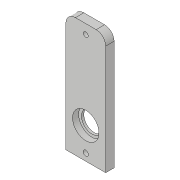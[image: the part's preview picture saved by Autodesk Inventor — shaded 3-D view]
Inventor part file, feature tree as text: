
AUTODESK INVENTOR PART (.ipt)
format: ipt  version: 2018.3 (Build 223284000, 284)  size: 190,976 bytes
history: native  units: in
note: dims shown in document units (in); Inventor stores cm internally (conversion verified against a paired STEP export)
features: extrude x4, sketch x4, fillet x1
ambient origin geometry x8: Origin, YZ Plane, XZ Plane, XY Plane, X Axis, Y Axis, Z Axis, Center Point
bodies: Solid1 (feature_tree)
feature tree (9):
  extrude  "Extrusion1"  Depth=0.221in TaperAngle=0.0deg
  extrude  "Extrusion2"  Depth=0.221in TaperAngle=0.0deg
  extrude  "Extrusion3"  Depth=0.221in
  fillet  "Fillet1"  Radius=0.221in
  extrude  "Extrusion5"  Depth=1.0429in
  sketch  "Sketch1"  dims[d0=0.6925in d3=1.0429in d4=0.5215in d5=2.3125in d6=3.125in d8=0.221in d9=0.0in]
  sketch  "Sketch2"  dims[d10=0.126in d12=0.25in d13=0.221in d14=0.0in]
  sketch  "Sketch3"  dims[d15=0.125in d17=0.136in d18=0.628in d19=0.221in d20=0.0in]
  sketch  "Sketch5"  dims[d21=0.25in d25=1.0429in d26=0.5215in d27=0.5215in d28=0.545in d29=0.0625in d30=0.0in]
